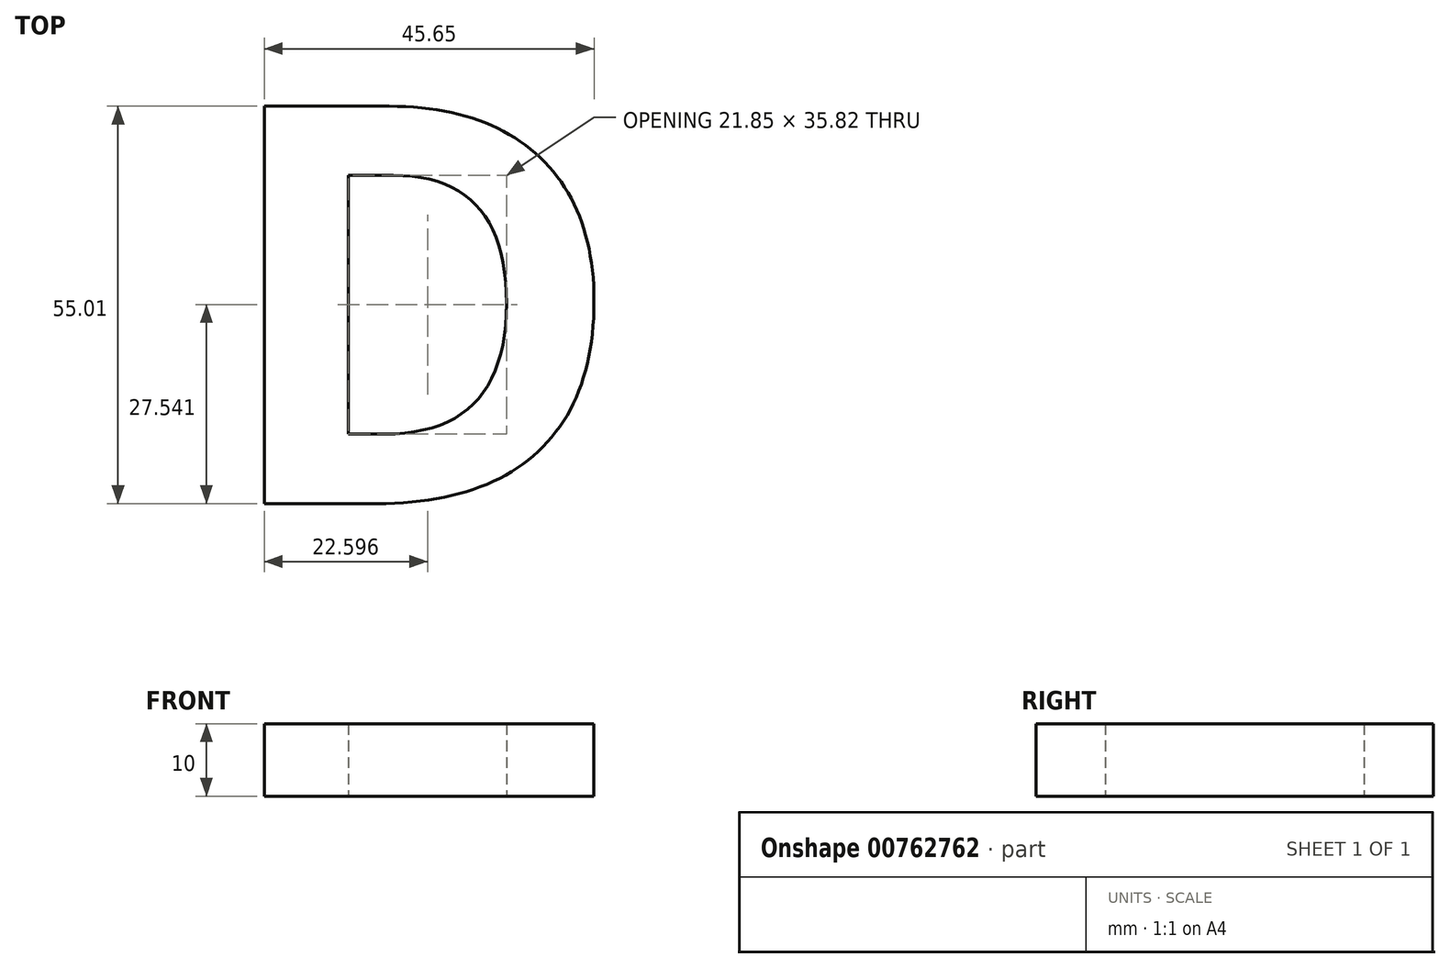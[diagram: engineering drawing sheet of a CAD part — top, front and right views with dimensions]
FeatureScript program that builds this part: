
annotation { "Feature Type Name" : "Feature", "Feature Type Description" : "" }
export const myFeature = defineFeature(function(context is Context, id is Id, definition is map)
    precondition{}
    {
        {
            var Q0;
            Q0=qCreatedBy(makeId("Top.planeOp"),FACE);
            var sketch = newSketch(context, id + "F0", { "sketchPlane" : qUnion([Q0])});
            skText(sketch, "E0", { "text": "D", "fontName": "OpenSans-Bold.ttf"});
            const initialGuessF0  = {"E0": [0, 0, 1, 0, 0.05548]};
            skSetInitialGuess(sketch, initialGuessF0);
            skSolve(sketch);
        }
        {
            var Q0;
            Q0 = qSketchRegion(id + "F0", true);
            extrude(context, id + "F1", {"entities" : qUnion([Q0]), "depth" : 10 * mm, "offsetDistance" : 25 * mm});
        }
    });
